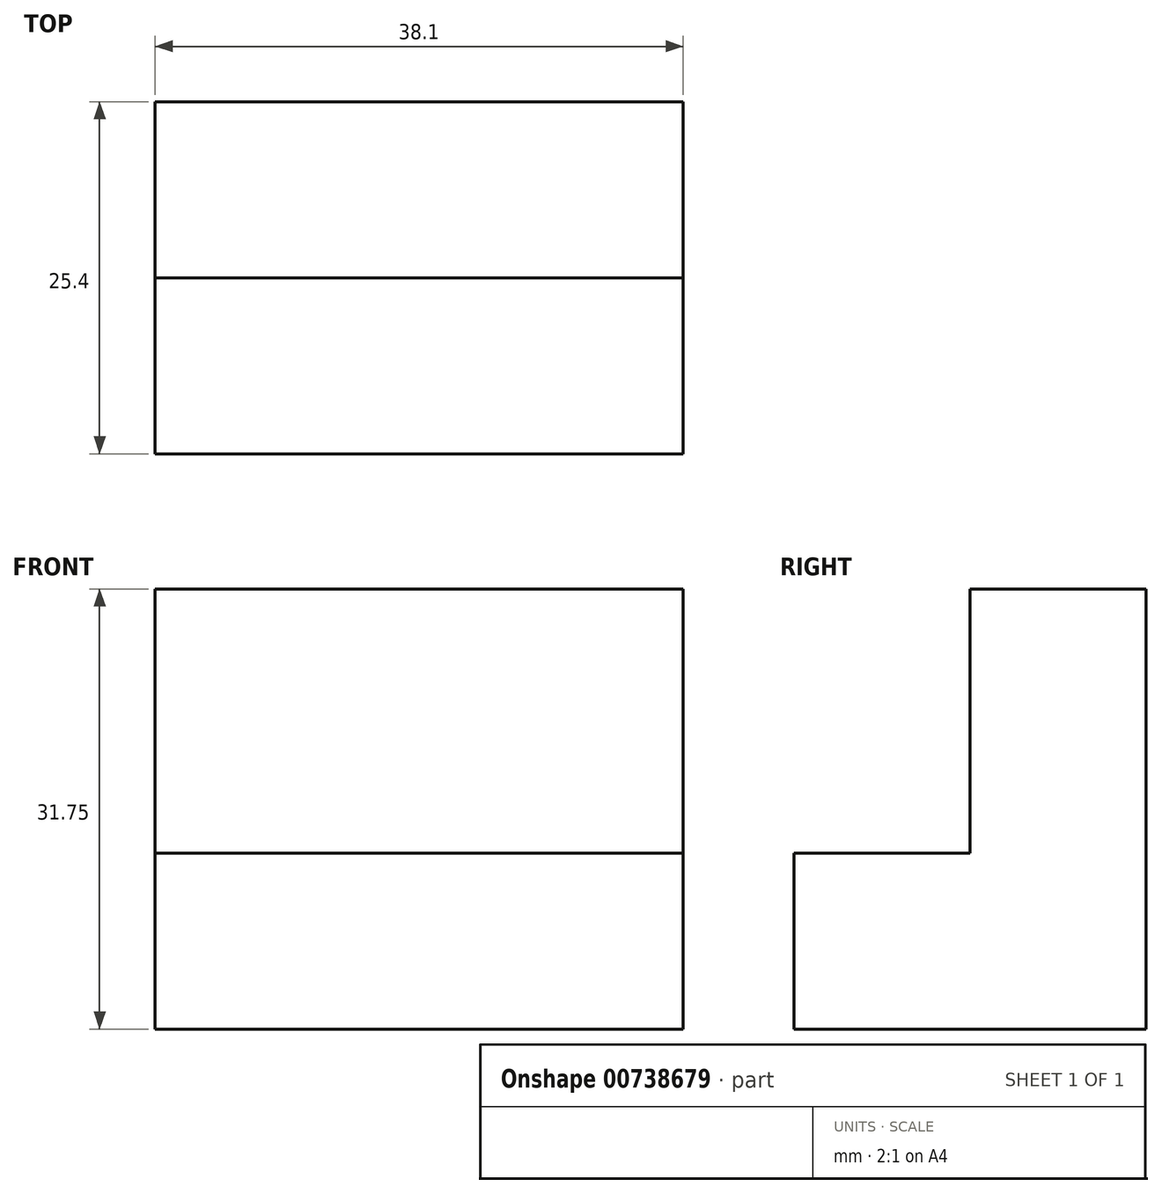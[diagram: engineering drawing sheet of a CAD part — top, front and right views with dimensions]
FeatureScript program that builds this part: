
annotation { "Feature Type Name" : "Feature", "Feature Type Description" : "" }
export const myFeature = defineFeature(function(context is Context, id is Id, definition is map)
    precondition{}
    {
        {
            var Q0;
            Q0=qCreatedBy(makeId("Right.planeOp"),FACE);
            var sketch = newSketch(context, id + "F0", { "sketchPlane" : qUnion([Q0])});
            skLineSegment(sketch, "E0", {"start": v(0, 31.75) * mm, "end": v(0, 0) * mm});
            skLineSegment(sketch, "E1", {"start": v(0, 0) * mm, "end": v(-25.4, 0) * mm});
            skLineSegment(sketch, "E2", {"start": v(-25.4, 0) * mm, "end": v(-25.4, 12.7) * mm});
            skLineSegment(sketch, "E3", {"start": v(-25.4, 12.7) * mm, "end": v(-12.7, 12.7) * mm});
            skLineSegment(sketch, "E4", {"start": v(-12.7, 12.7) * mm, "end": v(-12.7, 31.75) * mm});
            skLineSegment(sketch, "E5", {"start": v(-12.7, 31.75) * mm, "end": v(0, 31.75) * mm});
            skSolve(sketch);
        }
        {
            var Q0;
            Q0 = qSketchRegion(id + "F0", true);
            extrude(context, id + "F1", {"entities" : qUnion([Q0]), "depth" : 38.1 * mm, "offsetDistance" : 25.4 * mm});
        }
    });
